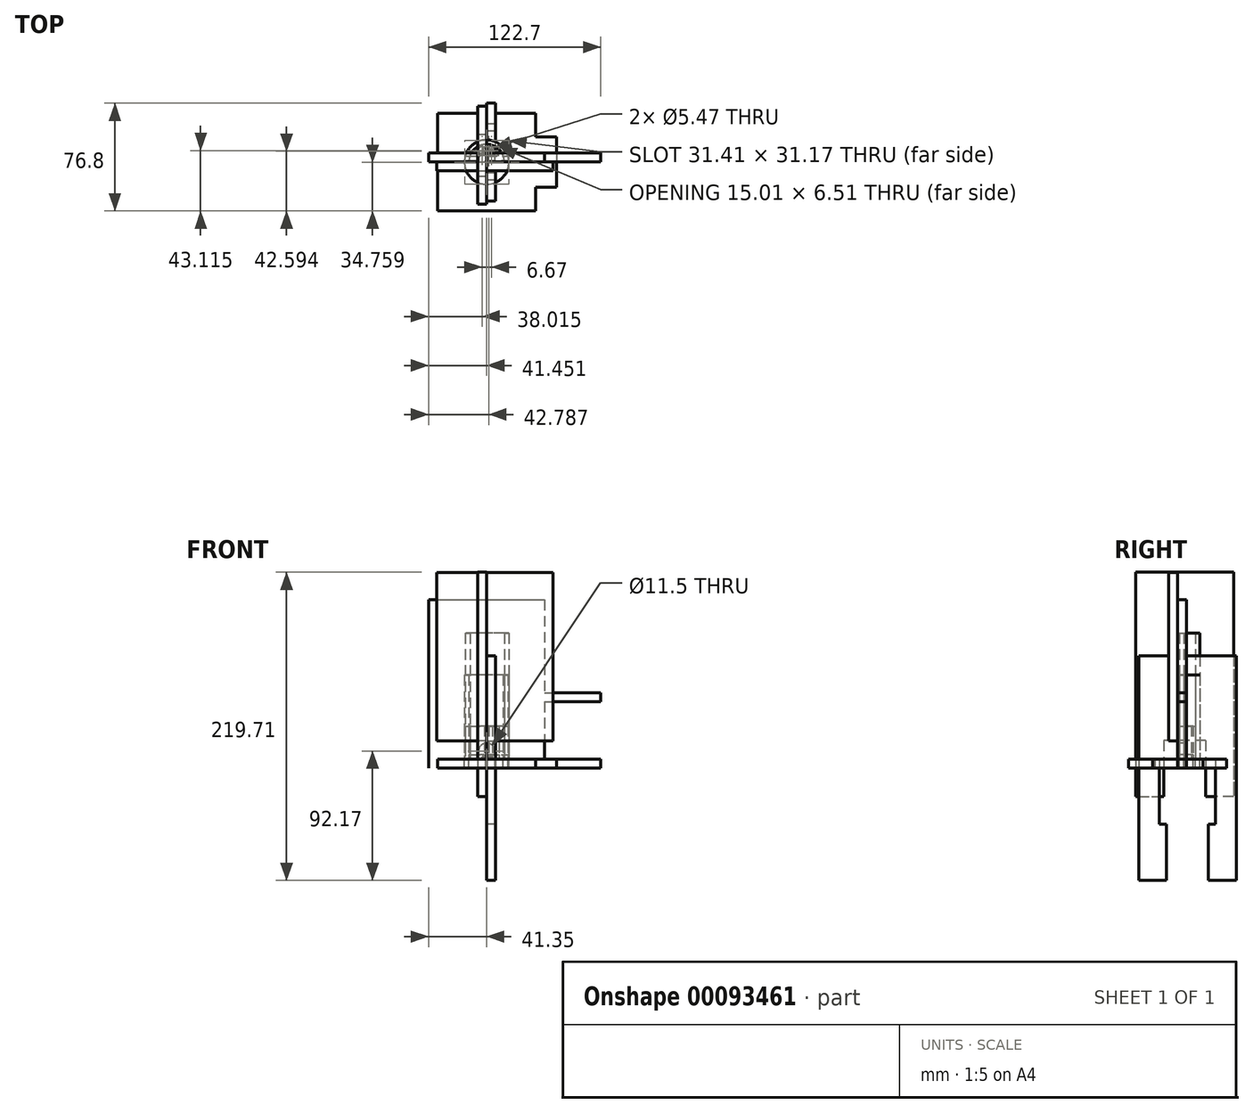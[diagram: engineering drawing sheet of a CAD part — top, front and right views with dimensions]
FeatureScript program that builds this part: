
annotation { "Feature Type Name" : "Feature", "Feature Type Description" : "" }
export const myFeature = defineFeature(function(context is Context, id is Id, definition is map)
    precondition{}
    {
        {
            var Q0;
            Q0=qCreatedBy(makeId("Top.planeOp"),FACE);
            var sketch = newSketch(context, id + "F0", { "sketchPlane" : qUnion([Q0])});
            skLineSegment(sketch, "E0.bottom", {"start": v(-34.9, 34.9) * mm, "end": v(34.9, 34.9) * mm});
            skLineSegment(sketch, "E0.top", {"start": v(-34.9, -34.9) * mm, "end": v(34.9, -34.9) * mm});
            skLineSegment(sketch, "E0.left", {"start": v(-34.9, 34.9) * mm, "end": v(-34.9, -34.9) * mm});
            skLineSegment(sketch, "E0.right", {"start": v(34.9, 34.9) * mm, "end": v(34.9, -34.9) * mm});
            skPoint(sketch, "E0.middle", {"position": v(0, 0) * mm});
            skCircle(sketch, "E1", {"center": v(0, 0) * mm, "radius": 15.85 * mm});
            skLineSegment(sketch, "E2.bottom", {"start": v(34.9, 18) * mm, "end": v(49.9, 18) * mm});
            skLineSegment(sketch, "E2.top", {"start": v(34.9, -18) * mm, "end": v(49.9, -18) * mm});
            skLineSegment(sketch, "E2.right", {"start": v(49.9, 18) * mm, "end": v(49.9, -18) * mm});
            skCircle(sketch, "E3", {"center": v(0, 0) * mm, "radius": 12.65 * mm});
            skPoint(sketch, "E4.startSnap0", {"position": v(-34.9, 0) * mm});
            skCircle(sketch, "E5", {"center": v(3.34, 8.21) * mm, "radius": 2.74 * mm});
            skCircle(sketch, "E6", {"center": v(-3.34, 8.21) * mm, "radius": 2.74 * mm});
            skCircle(sketch, "E7", {"center": v(0, 8.21) * mm, "radius": 2.74 * mm});
            skCircle(sketch, "E8", {"center": v(6.26, 7.15) * mm, "radius": 2.74 * mm});
            skLineSegment(sketch, "E9", {"start": v(3.63, 6.39) * mm, "end": v(8.89, 6.39) * mm});
            skLineSegment(sketch, "E10", {"start": v(-15.24, 4.35) * mm, "end": v(15.24, 4.35) * mm});
            skLineSegment(sketch, "E11", {"start": v(-15.8, 1.17) * mm, "end": v(15.8, 1.17) * mm});
            skSolve(sketch);
        }
        {
            var Q0;
            {var subQ0=sQuery(id+"F0.wireOp",EDGE,"E2.bottom");Q0=makeQuery(id+"F0.imprint","IMPRINT",FACE,{"disambiguationData":[TD([[makeQuery(id+"F0.imprint","IMPRINT",EDGE,{"derivedFrom":subQ0}),-1.0]])]});}
            var Q1;
            {var subQ1=sQuery(id+"F0.wireOp",EDGE,"E0.bottom");Q1=makeQuery(id+"F0.imprint","IMPRINT",FACE,{"disambiguationData":[TD([[makeQuery(id+"F0.imprint","IMPRINT",EDGE,{"derivedFrom":subQ1}),-1.0]])]});}
            var Q2;
            {var subQ0=sQuery(id+"F0.wireOp",EDGE,"E7");var subQ1=sQuery(id+"F0.wireOp",EDGE,"E5");var subQ2=makeQuery(id+"F0.imprint","INTERSECT",VERTEX,{"disambiguationData":[OD(0.0)],"derivedFrom":[subQ1,subQ0]});Q2=makeQuery(id+"F0.imprint","IMPRINT",FACE,{"disambiguationData":[TD([[makeQuery(id+"F0.imprint","IMPRINT",EDGE,{"disambiguationData":[TD([[subQ2,-1.0]])],"derivedFrom":subQ1}),-1.0]])]});}
            var Q3;
            {var subQ0=sQuery(id+"F0.wireOp",EDGE,"E8");var subQ1=sQuery(id+"F0.wireOp",EDGE,"E5");var subQ2=makeQuery(id+"F0.imprint","INTERSECT",VERTEX,{"disambiguationData":[OD(0.0)],"derivedFrom":[subQ1,subQ0]});Q3=makeQuery(id+"F0.imprint","IMPRINT",FACE,{"disambiguationData":[TD([[makeQuery(id+"F0.imprint","IMPRINT",EDGE,{"disambiguationData":[TD([[subQ2,1.0]])],"derivedFrom":subQ1}),-1.0]])]});}
            var Q4;
            {var subQ0=sQuery(id+"F0.wireOp",EDGE,"E10");var subQ1=sQuery(id+"F0.wireOp",EDGE,"E1");var subQ2=makeQuery(id+"F0.imprint","INTERSECT",VERTEX,{"disambiguationData":[OD(0.0)],"derivedFrom":[subQ1,subQ0]});Q4=makeQuery(id+"F0.imprint","IMPRINT",FACE,{"disambiguationData":[TD([[makeQuery(id+"F0.imprint","IMPRINT",EDGE,{"disambiguationData":[TD([[subQ2,1.0]])],"derivedFrom":subQ1}),1.0]])]});}
            var Q5;
            {var subQ11=sQuery(id+"F0.wireOp",EDGE,"E10");var subQ12=sQuery(id+"F0.wireOp",EDGE,"E3");var subQ13=makeQuery(id+"F0.imprint","INTERSECT",VERTEX,{"disambiguationData":[OD(0.0)],"derivedFrom":[subQ12,subQ11]});Q5=makeQuery(id+"F0.imprint","IMPRINT",FACE,{"disambiguationData":[TD([[makeQuery(id+"F0.imprint","IMPRINT",EDGE,{"disambiguationData":[TD([[subQ13,-1.0]])],"derivedFrom":subQ12}),1.0]])]});}
            var Q6;
            {var subQ0=sQuery(id+"F0.wireOp",EDGE,"E10");var subQ1=sQuery(id+"F0.wireOp",EDGE,"E3");var subQ2=makeQuery(id+"F0.imprint","INTERSECT",VERTEX,{"disambiguationData":[OD(0.0)],"derivedFrom":[subQ1,subQ0]});Q6=makeQuery(id+"F0.imprint","IMPRINT",FACE,{"disambiguationData":[TD([[makeQuery(id+"F0.imprint","IMPRINT",EDGE,{"disambiguationData":[TD([[subQ2,1.0]])],"derivedFrom":subQ1}),1.0]])]});}
            var Q7;
            {var subQ0=sQuery(id+"F0.wireOp",EDGE,"E8");var subQ1=sQuery(id+"F0.wireOp",EDGE,"E5");var subQ2=makeQuery(id+"F0.imprint","INTERSECT",VERTEX,{"disambiguationData":[OD(1.0)],"derivedFrom":[subQ1,subQ0]});Q7=makeQuery(id+"F0.imprint","IMPRINT",FACE,{"disambiguationData":[TD([[makeQuery(id+"F0.imprint","IMPRINT",EDGE,{"disambiguationData":[TD([[subQ2,-1.0]])],"derivedFrom":subQ1}),-1.0]])]});}
            extrude(context, id + "F1", {"entities" : qUnion([Q0, Q1, Q2, Q3, Q4, Q5, Q6, Q7]), "oppositeDirection" : true, "depth" : 6.35 * mm});
        }
        {
            var Q0;
            Q0=qCreatedBy(makeId("Front.planeOp"),FACE);
            var sketch = newSketch(context, id + "F2", { "sketchPlane" : qUnion([Q0])});
            skLineSegment(sketch, "E12.bottom", {"start": v(-35.54, 133.25) * mm, "end": v(47.16, 133.25) * mm});
            skLineSegment(sketch, "E12.top", {"start": v(-35.54, 13.25) * mm, "end": v(47.16, 13.25) * mm});
            skLineSegment(sketch, "E12.left", {"start": v(-35.54, 133.25) * mm, "end": v(-35.54, 13.25) * mm});
            skLineSegment(sketch, "E12.right", {"start": v(47.16, 133.25) * mm, "end": v(47.16, 13.25) * mm});
            skLineSegment(sketch, "E13.bottom", {"start": v(-35.54, 13.25) * mm, "end": v(-9.2, 13.25) * mm});
            skLineSegment(sketch, "E13.top", {"start": v(-35.54, -26.75) * mm, "end": v(-9.2, -26.75) * mm});
            skLineSegment(sketch, "E13.left", {"start": v(-35.54, 13.25) * mm, "end": v(-35.54, -26.75) * mm});
            skLineSegment(sketch, "E13.right", {"start": v(-9.2, 13.25) * mm, "end": v(-9.2, -26.75) * mm});
            skLineSegment(sketch, "E14.bottom", {"start": v(47.16, 13.25) * mm, "end": v(20.8, 13.25) * mm});
            skLineSegment(sketch, "E14.top", {"start": v(47.16, -26.75) * mm, "end": v(20.8, -26.75) * mm});
            skLineSegment(sketch, "E14.left", {"start": v(47.16, 13.25) * mm, "end": v(47.16, -26.75) * mm});
            skLineSegment(sketch, "E14.right", {"start": v(20.8, 13.25) * mm, "end": v(20.8, -26.75) * mm});
            skSolve(sketch);
        }
        {
            var Q0;
            Q0=makeQuery(id+"F2.imprint","IMPRINT",FACE,{"disambiguationData":[TD([[makeQuery(id+"F2.imprint","IMPRINT",EDGE,{"derivedFrom":sQuery(id+"F2.wireOp",EDGE,"E13.bottom")}),-1.0]])]});
            var Q1;
            Q1=makeQuery(id+"F2.imprint","IMPRINT",FACE,{"disambiguationData":[TD([[makeQuery(id+"F2.imprint","IMPRINT",EDGE,{"derivedFrom":sQuery(id+"F2.wireOp",EDGE,"E14.bottom")}),1.0]])]});
            var Q2;
            Q2=makeQuery(id+"F2.imprint","IMPRINT",FACE,{"disambiguationData":[TD([[makeQuery(id+"F2.imprint","IMPRINT",EDGE,{"derivedFrom":sQuery(id+"F2.wireOp",EDGE,"E12.bottom")}),-1.0]])]});
            extrude(context, id + "F3", {"entities" : qUnion([Q0, Q1, Q2]), "depth" : 6.35 * mm});
        }
        {
            var Q0;
            Q0=qCreatedBy(makeId("Front.planeOp"),FACE);
            var sketch = newSketch(context, id + "F4", { "sketchPlane" : qUnion([Q0])});
            skLineSegment(sketch, "E15.bottom", {"start": v(-41.35, 113.65) * mm, "end": v(41.35, 113.65) * mm});
            skLineSegment(sketch, "E15.top", {"start": v(-41.35, -6.35) * mm, "end": v(41.35, -6.35) * mm});
            skLineSegment(sketch, "E15.left", {"start": v(-41.35, 113.65) * mm, "end": v(-41.35, -6.35) * mm});
            skLineSegment(sketch, "E15.right", {"start": v(41.35, 113.65) * mm, "end": v(41.35, -6.35) * mm});
            skLineSegment(sketch, "E16.bottom", {"start": v(-41.35, -6.35) * mm, "end": v(-15, -6.35) * mm});
            skLineSegment(sketch, "E16.top", {"start": v(-41.35, -46.35) * mm, "end": v(-15, -46.35) * mm});
            skLineSegment(sketch, "E16.left", {"start": v(-41.35, -6.35) * mm, "end": v(-41.35, -46.35) * mm});
            skLineSegment(sketch, "E16.right", {"start": v(-15, -6.35) * mm, "end": v(-15, -46.35) * mm});
            skLineSegment(sketch, "E17.bottom", {"start": v(41.35, -6.35) * mm, "end": v(15, -6.35) * mm});
            skLineSegment(sketch, "E17.top", {"start": v(41.35, -46.35) * mm, "end": v(15, -46.35) * mm});
            skLineSegment(sketch, "E17.left", {"start": v(41.35, -6.35) * mm, "end": v(41.35, -46.35) * mm});
            skLineSegment(sketch, "E17.right", {"start": v(15, -6.35) * mm, "end": v(15, -46.35) * mm});
            skCircle(sketch, "E18", {"center": v(0, 5.8) * mm, "radius": 5.75 * mm});
            skLineSegment(sketch, "E19.bottom", {"start": v(41.35, -6.35) * mm, "end": v(81.35, -6.35) * mm});
            skLineSegment(sketch, "E19.top", {"start": v(41.35, 47.35) * mm, "end": v(81.35, 47.35) * mm});
            skLineSegment(sketch, "E19.left", {"start": v(41.35, -6.35) * mm, "end": v(41.35, 47.35) * mm});
            skLineSegment(sketch, "E19.right", {"start": v(81.35, -6.35) * mm, "end": v(81.35, 47.35) * mm});
            skLineSegment(sketch, "E20.bottom", {"start": v(41.35, 41) * mm, "end": v(81.35, 41) * mm});
            skLineSegment(sketch, "E20.top", {"start": v(41.35, 0) * mm, "end": v(81.35, 0) * mm});
            skLineSegment(sketch, "E20.left", {"start": v(41.35, 41) * mm, "end": v(41.35, 0) * mm});
            skLineSegment(sketch, "E20.right", {"start": v(81.35, 41) * mm, "end": v(81.35, 0) * mm});
            skSolve(sketch);
        }
        {
            var Q0;
            Q0=makeQuery(id+"F4.imprint","IMPRINT",FACE,{"disambiguationData":[TD([[makeQuery(id+"F4.imprint","IMPRINT",EDGE,{"derivedFrom":sQuery(id+"F4.wireOp",EDGE,"E16.bottom")}),-1.0]])]});
            var Q1;
            Q1=makeQuery(id+"F4.imprint","IMPRINT",FACE,{"disambiguationData":[TD([[makeQuery(id+"F4.imprint","IMPRINT",EDGE,{"derivedFrom":sQuery(id+"F4.wireOp",EDGE,"E17.bottom")}),1.0]])]});
            var Q2;
            Q2=makeQuery(id+"F4.imprint","IMPRINT",FACE,{"disambiguationData":[TD([[makeQuery(id+"F4.imprint","IMPRINT",EDGE,{"derivedFrom":sQuery(id+"F4.wireOp",EDGE,"E15.bottom")}),-1.0]])]});
            var Q3;
            {var subQ0=sQuery(id+"F4.wireOp",EDGE,"E19.bottom");Q3=makeQuery(id+"F4.imprint","IMPRINT",FACE,{"disambiguationData":[TD([[makeQuery(id+"F4.imprint","IMPRINT",EDGE,{"derivedFrom":subQ0}),1.0]])]});}
            var Q4;
            {var subQ0=sQuery(id+"F4.wireOp",EDGE,"E19.top");Q4=makeQuery(id+"F4.imprint","IMPRINT",FACE,{"disambiguationData":[TD([[makeQuery(id+"F4.imprint","IMPRINT",EDGE,{"derivedFrom":subQ0}),-1.0]])]});}
            extrude(context, id + "F5", {"entities" : qUnion([Q0, Q1, Q2, Q3, Q4]), "oppositeDirection" : true, "depth" : 6.35 * mm});
        }
        {
            var Q0;
            Q0=qCreatedBy(makeId("Right.planeOp"),FACE);
            var sketch = newSketch(context, id + "F6", { "sketchPlane" : qUnion([Q0])});
            skLineSegment(sketch, "E21.bottom", {"start": v(39.82, 133.34) * mm, "end": v(-29.98, 133.34) * mm});
            skLineSegment(sketch, "E21.top", {"start": v(39.82, 13.34) * mm, "end": v(-29.98, 13.34) * mm});
            skLineSegment(sketch, "E21.left", {"start": v(39.82, 133.34) * mm, "end": v(39.82, 13.34) * mm});
            skLineSegment(sketch, "E21.right", {"start": v(-29.98, 133.34) * mm, "end": v(-29.98, 13.34) * mm});
            skLineSegment(sketch, "E22.bottom", {"start": v(39.82, 13.34) * mm, "end": v(19.82, 13.34) * mm});
            skLineSegment(sketch, "E22.top", {"start": v(39.82, -26.66) * mm, "end": v(19.82, -26.66) * mm});
            skLineSegment(sketch, "E22.left", {"start": v(39.82, 13.34) * mm, "end": v(39.82, -26.66) * mm});
            skLineSegment(sketch, "E22.right", {"start": v(19.82, 13.34) * mm, "end": v(19.82, -26.66) * mm});
            skLineSegment(sketch, "E23.bottom", {"start": v(-29.98, 13.34) * mm, "end": v(-9.98, 13.34) * mm});
            skLineSegment(sketch, "E23.top", {"start": v(-29.98, -26.66) * mm, "end": v(-9.98, -26.66) * mm});
            skLineSegment(sketch, "E23.left", {"start": v(-29.98, 13.34) * mm, "end": v(-29.98, -26.66) * mm});
            skLineSegment(sketch, "E23.right", {"start": v(-9.98, 13.34) * mm, "end": v(-9.98, -26.66) * mm});
            skSolve(sketch);
        }
        {
            var Q0;
            Q0 = qSketchRegion(id + "F6", true);
            extrude(context, id + "F7", {"entities" : qUnion([Q0]), "oppositeDirection" : true, "depth" : 6.35 * mm});
        }
        {
            var Q0;
            Q0=qCreatedBy(makeId("Right.planeOp"),FACE);
            var sketch = newSketch(context, id + "F8", { "sketchPlane" : qUnion([Q0])});
            skLineSegment(sketch, "E24.bottom", {"start": v(-27.9, 73.63) * mm, "end": v(41.9, 73.63) * mm});
            skLineSegment(sketch, "E24.top", {"start": v(-27.9, -46.37) * mm, "end": v(41.9, -46.37) * mm});
            skLineSegment(sketch, "E24.left", {"start": v(-27.9, 73.63) * mm, "end": v(-27.9, -46.37) * mm});
            skLineSegment(sketch, "E24.right", {"start": v(41.9, 73.63) * mm, "end": v(41.9, -46.37) * mm});
            skLineSegment(sketch, "E25.bottom", {"start": v(-13, 0) * mm, "end": v(27, 0) * mm});
            skLineSegment(sketch, "E25.top", {"start": v(-13, -46.37) * mm, "end": v(27, -46.37) * mm});
            skLineSegment(sketch, "E25.left", {"start": v(-13, 0) * mm, "end": v(-13, -46.37) * mm});
            skLineSegment(sketch, "E25.right", {"start": v(27, 0) * mm, "end": v(27, -46.37) * mm});
            skLineSegment(sketch, "E26.bottom", {"start": v(-27.9, -46.37) * mm, "end": v(-7.9, -46.37) * mm});
            skLineSegment(sketch, "E26.top", {"start": v(-27.9, -86.37) * mm, "end": v(-7.9, -86.37) * mm});
            skLineSegment(sketch, "E26.left", {"start": v(-27.9, -46.37) * mm, "end": v(-27.9, -86.37) * mm});
            skLineSegment(sketch, "E26.right", {"start": v(-7.9, -46.37) * mm, "end": v(-7.9, -86.37) * mm});
            skLineSegment(sketch, "E27.bottom", {"start": v(41.9, -46.37) * mm, "end": v(21.9, -46.37) * mm});
            skLineSegment(sketch, "E27.top", {"start": v(41.9, -86.37) * mm, "end": v(21.9, -86.37) * mm});
            skLineSegment(sketch, "E27.left", {"start": v(41.9, -46.37) * mm, "end": v(41.9, -86.37) * mm});
            skLineSegment(sketch, "E27.right", {"start": v(21.9, -46.37) * mm, "end": v(21.9, -86.37) * mm});
            skSolve(sketch);
        }
        {
            var Q0;
            Q0=makeQuery(id+"F8.imprint","IMPRINT",FACE,{"disambiguationData":[TD([[makeQuery(id+"F8.imprint","IMPRINT",EDGE,{"derivedFrom":sQuery(id+"F8.wireOp",EDGE,"E26.top")}),1.0]])]});
            var Q1;
            Q1=makeQuery(id+"F8.imprint","IMPRINT",FACE,{"disambiguationData":[TD([[makeQuery(id+"F8.imprint","IMPRINT",EDGE,{"derivedFrom":sQuery(id+"F8.wireOp",EDGE,"E27.top")}),-1.0]])]});
            var Q2;
            Q2=makeQuery(id+"F8.imprint","IMPRINT",FACE,{"disambiguationData":[TD([[makeQuery(id+"F8.imprint","IMPRINT",EDGE,{"derivedFrom":sQuery(id+"F8.wireOp",EDGE,"E24.bottom")}),-1.0]])]});
            extrude(context, id + "F9", {"entities" : qUnion([Q0, Q1, Q2]), "depth" : 6.35 * mm});
        }
        {
            var Q0;
            {var subQ0=sQuery(id+"F0.wireOp",EDGE,"E10");var subQ1=sQuery(id+"F0.wireOp",EDGE,"E1");var subQ2=makeQuery(id+"F0.imprint","INTERSECT",VERTEX,{"disambiguationData":[OD(0.0)],"derivedFrom":[subQ1,subQ0]});Q0=makeQuery(id+"F0.imprint","IMPRINT",FACE,{"disambiguationData":[TD([[makeQuery(id+"F0.imprint","IMPRINT",EDGE,{"disambiguationData":[TD([[subQ2,1.0]])],"derivedFrom":subQ1}),1.0]])]});}
            var Q1;
            {var subQ0=sQuery(id+"F0.wireOp",EDGE,"E10");var subQ1=sQuery(id+"F0.wireOp",EDGE,"E1");var subQ2=makeQuery(id+"F0.imprint","INTERSECT",VERTEX,{"disambiguationData":[OD(1.0)],"derivedFrom":[subQ1,subQ0]});Q1=makeQuery(id+"F0.imprint","IMPRINT",FACE,{"disambiguationData":[TD([[makeQuery(id+"F0.imprint","IMPRINT",EDGE,{"disambiguationData":[TD([[subQ2,-1.0]])],"derivedFrom":subQ1}),1.0]])]});}
            var Q2;
            {var subQ0=sQuery(id+"F0.wireOp",EDGE,"E10");var subQ1=sQuery(id+"F0.wireOp",EDGE,"E1");var subQ2=makeQuery(id+"F0.imprint","INTERSECT",VERTEX,{"disambiguationData":[OD(0.0)],"derivedFrom":[subQ1,subQ0]});Q2=makeQuery(id+"F0.imprint","IMPRINT",FACE,{"disambiguationData":[TD([[makeQuery(id+"F0.imprint","IMPRINT",EDGE,{"disambiguationData":[TD([[subQ2,1.0]])],"derivedFrom":subQ1}),1.0]])]});}
            var Q3;
            {var subQ0=sQuery(id+"F0.wireOp",EDGE,"E10");var subQ1=sQuery(id+"F0.wireOp",EDGE,"E1");var subQ2=makeQuery(id+"F0.imprint","INTERSECT",VERTEX,{"disambiguationData":[OD(0.0)],"derivedFrom":[subQ1,subQ0]});Q3=makeQuery(id+"F0.imprint","IMPRINT",FACE,{"disambiguationData":[TD([[makeQuery(id+"F0.imprint","IMPRINT",EDGE,{"disambiguationData":[TD([[subQ2,1.0]])],"derivedFrom":subQ1}),1.0]])]});}
            var Q4;
            {var subQ0=sQuery(id+"F0.wireOp",EDGE,"E10");var subQ1=sQuery(id+"F0.wireOp",EDGE,"E1");var subQ2=makeQuery(id+"F0.imprint","INTERSECT",VERTEX,{"disambiguationData":[OD(1.0)],"derivedFrom":[subQ1,subQ0]});Q4=makeQuery(id+"F0.imprint","IMPRINT",FACE,{"disambiguationData":[TD([[makeQuery(id+"F0.imprint","IMPRINT",EDGE,{"disambiguationData":[TD([[subQ2,-1.0]])],"derivedFrom":subQ1}),1.0]])]});}
            var Q5;
            {var subQ0=sQuery(id+"F0.wireOp",EDGE,"n6fMbl8c-e2gG-Q103-9a3W-R0qhI9RANw06");var subQ1=sQuery(id+"F0.wireOp",EDGE,"E3");var subQ2=makeQuery(id+"F0.imprint","INTERSECT",VERTEX,{"disambiguationData":[OD(0.0)],"derivedFrom":[subQ1,subQ0]});Q5=makeQuery(id+"F0.imprint","IMPRINT",FACE,{"disambiguationData":[TD([[makeQuery(id+"F0.imprint","IMPRINT",EDGE,{"disambiguationData":[TD([[subQ2,1.0]])],"derivedFrom":subQ1}),1.0]])]});}
            var Q6;
            {var subQ0=sQuery(id+"F0.wireOp",EDGE,"n6fMbl8c-e2gG-Q103-9a3W-R0qhI9RANw06");var subQ1=sQuery(id+"F0.wireOp",EDGE,"E8");var subQ2=makeQuery(id+"F0.imprint","INTERSECT",VERTEX,{"disambiguationData":[OD(0.0)],"derivedFrom":[subQ1,subQ0]});Q6=makeQuery(id+"F0.imprint","IMPRINT",FACE,{"disambiguationData":[TD([[makeQuery(id+"F0.imprint","IMPRINT",EDGE,{"disambiguationData":[TD([[subQ2,-1.0]])],"derivedFrom":subQ1}),1.0]])]});}
            extrude(context, id + "F10", {"entities" : qUnion([Q0, Q1, Q2, Q3, Q4, Q5, Q6]), "depth" : 23.7 * mm});
        }
        {
            var Q0;
            {var subQ0=sQuery(id+"F0.wireOp",EDGE,"E10");var subQ1=sQuery(id+"F0.wireOp",EDGE,"E1");var subQ2=makeQuery(id+"F0.imprint","INTERSECT",VERTEX,{"disambiguationData":[OD(0.0)],"derivedFrom":[subQ1,subQ0]});Q0=makeQuery(id+"F0.imprint","IMPRINT",FACE,{"disambiguationData":[TD([[makeQuery(id+"F0.imprint","IMPRINT",EDGE,{"disambiguationData":[TD([[subQ2,1.0]])],"derivedFrom":subQ1}),1.0]])]});}
            var Q1;
            {var subQ0=sQuery(id+"F0.wireOp",EDGE,"E10");var subQ1=sQuery(id+"F0.wireOp",EDGE,"E1");var subQ2=makeQuery(id+"F0.imprint","INTERSECT",VERTEX,{"disambiguationData":[OD(0.0)],"derivedFrom":[subQ1,subQ0]});Q1=makeQuery(id+"F0.imprint","IMPRINT",FACE,{"disambiguationData":[TD([[makeQuery(id+"F0.imprint","IMPRINT",EDGE,{"disambiguationData":[TD([[subQ2,1.0]])],"derivedFrom":subQ1}),1.0]])]});}
            var Q2;
            {var subQ0=sQuery(id+"F0.wireOp",EDGE,"E7");var subQ1=sQuery(id+"F0.wireOp",EDGE,"E6");var subQ2=makeQuery(id+"F0.imprint","INTERSECT",VERTEX,{"disambiguationData":[OD(0.0)],"derivedFrom":[subQ1,subQ0]});Q2=makeQuery(id+"F0.imprint","IMPRINT",FACE,{"disambiguationData":[TD([[makeQuery(id+"F0.imprint","IMPRINT",EDGE,{"disambiguationData":[TD([[subQ2,-1.0]])],"derivedFrom":subQ1}),1.0]])]});}
            var Q3;
            {var subQ2=sQuery(id+"F0.wireOp",EDGE,"E5");var subQ4=sQuery(id+"F0.wireOp",EDGE,"E7");var subQ5=makeQuery(id+"F0.imprint","INTERSECT",VERTEX,{"disambiguationData":[OD(0.0)],"derivedFrom":[subQ2,subQ4]});Q3=makeQuery(id+"F0.imprint","IMPRINT",FACE,{"disambiguationData":[TD([[makeQuery(id+"F0.imprint","IMPRINT",EDGE,{"disambiguationData":[TD([[subQ5,1.0]])],"derivedFrom":subQ2}),1.0]])]});}
            var Q4;
            {var subQ0=sQuery(id+"F0.wireOp",EDGE,"E8");var subQ1=sQuery(id+"F0.wireOp",EDGE,"E5");var subQ2=makeQuery(id+"F0.imprint","INTERSECT",VERTEX,{"disambiguationData":[OD(1.0)],"derivedFrom":[subQ1,subQ0]});Q4=makeQuery(id+"F0.imprint","IMPRINT",FACE,{"disambiguationData":[TD([[makeQuery(id+"F0.imprint","IMPRINT",EDGE,{"disambiguationData":[TD([[subQ2,-1.0]])],"derivedFrom":subQ1}),1.0]])]});}
            var Q5;
            {var subQ0=sQuery(id+"F0.wireOp",EDGE,"E8");var subQ1=sQuery(id+"F0.wireOp",EDGE,"E5");var subQ2=makeQuery(id+"F0.imprint","INTERSECT",VERTEX,{"disambiguationData":[OD(1.0)],"derivedFrom":[subQ1,subQ0]});Q5=makeQuery(id+"F0.imprint","IMPRINT",FACE,{"disambiguationData":[TD([[makeQuery(id+"F0.imprint","IMPRINT",EDGE,{"disambiguationData":[TD([[subQ2,-1.0]])],"derivedFrom":subQ1}),1.0]])]});}
            var Q6;
            {var subQ0=sQuery(id+"F0.wireOp",EDGE,"E10");var subQ1=sQuery(id+"F0.wireOp",EDGE,"E1");var subQ2=makeQuery(id+"F0.imprint","INTERSECT",VERTEX,{"disambiguationData":[OD(0.0)],"derivedFrom":[subQ1,subQ0]});Q6=makeQuery(id+"F0.imprint","IMPRINT",FACE,{"disambiguationData":[TD([[makeQuery(id+"F0.imprint","IMPRINT",EDGE,{"disambiguationData":[TD([[subQ2,1.0]])],"derivedFrom":subQ1}),1.0]])]});}
            var Q7;
            {var subQ11=sQuery(id+"F0.wireOp",EDGE,"E10");var subQ12=sQuery(id+"F0.wireOp",EDGE,"E3");var subQ13=makeQuery(id+"F0.imprint","INTERSECT",VERTEX,{"disambiguationData":[OD(0.0)],"derivedFrom":[subQ12,subQ11]});Q7=makeQuery(id+"F0.imprint","IMPRINT",FACE,{"disambiguationData":[TD([[makeQuery(id+"F0.imprint","IMPRINT",EDGE,{"disambiguationData":[TD([[subQ13,-1.0]])],"derivedFrom":subQ12}),1.0]])]});}
            var Q8;
            {var subQ0=sQuery(id+"F0.wireOp",EDGE,"E8");var subQ1=sQuery(id+"F0.wireOp",EDGE,"E5");var subQ2=makeQuery(id+"F0.imprint","INTERSECT",VERTEX,{"disambiguationData":[OD(1.0)],"derivedFrom":[subQ1,subQ0]});Q8=makeQuery(id+"F0.imprint","IMPRINT",FACE,{"disambiguationData":[TD([[makeQuery(id+"F0.imprint","IMPRINT",EDGE,{"disambiguationData":[TD([[subQ2,-1.0]])],"derivedFrom":subQ1}),-1.0]])]});}
            extrude(context, id + "F11", {"entities" : qUnion([Q0, Q1, Q2, Q3, Q4, Q5, Q6, Q7, Q8]), "depth" : 3.17 * mm});
        }
        {
            var Q0;
            {var subQ0=sQuery(id+"F0.wireOp",EDGE,"E10");var subQ1=sQuery(id+"F0.wireOp",EDGE,"E3");var subQ2=makeQuery(id+"F0.imprint","INTERSECT",VERTEX,{"disambiguationData":[OD(0.0)],"derivedFrom":[subQ1,subQ0]});Q0=makeQuery(id+"F0.imprint","IMPRINT",FACE,{"disambiguationData":[TD([[makeQuery(id+"F0.imprint","IMPRINT",EDGE,{"disambiguationData":[TD([[subQ2,1.0]])],"derivedFrom":subQ1}),1.0]])]});}
            extrude(context, id + "F12", {"entities" : qUnion([Q0]), "depth" : 23.65 * mm});
        }
        {
            var Q0;
            {var subQ0=sQuery(id+"F0.wireOp",EDGE,"E10");var subQ1=sQuery(id+"F0.wireOp",EDGE,"E1");var subQ2=makeQuery(id+"F0.imprint","INTERSECT",VERTEX,{"disambiguationData":[OD(0.0)],"derivedFrom":[subQ1,subQ0]});Q0=makeQuery(id+"F0.imprint","IMPRINT",FACE,{"disambiguationData":[TD([[makeQuery(id+"F0.imprint","IMPRINT",EDGE,{"disambiguationData":[TD([[subQ2,1.0]])],"derivedFrom":subQ1}),1.0]])]});}
            var Q1;
            {var subQ0=sQuery(id+"F0.wireOp",EDGE,"E10");var subQ1=sQuery(id+"F0.wireOp",EDGE,"E1");var subQ2=makeQuery(id+"F0.imprint","INTERSECT",VERTEX,{"disambiguationData":[OD(0.0)],"derivedFrom":[subQ1,subQ0]});Q1=makeQuery(id+"F0.imprint","IMPRINT",FACE,{"disambiguationData":[TD([[makeQuery(id+"F0.imprint","IMPRINT",EDGE,{"disambiguationData":[TD([[subQ2,-1.0]])],"derivedFrom":subQ1}),1.0]])]});}
            var Q2;
            {var subQ0=sQuery(id+"F0.wireOp",EDGE,"E10");var subQ1=sQuery(id+"F0.wireOp",EDGE,"E1");var subQ2=makeQuery(id+"F0.imprint","INTERSECT",VERTEX,{"disambiguationData":[OD(1.0)],"derivedFrom":[subQ1,subQ0]});Q2=makeQuery(id+"F0.imprint","IMPRINT",FACE,{"disambiguationData":[TD([[makeQuery(id+"F0.imprint","IMPRINT",EDGE,{"disambiguationData":[TD([[subQ2,-1.0]])],"derivedFrom":subQ1}),1.0]])]});}
            var Q3;
            {var subQ0=sQuery(id+"F0.wireOp",EDGE,"n6fMbl8c-e2gG-Q103-9a3W-R0qhI9RANw06");var subQ1=sQuery(id+"F0.wireOp",EDGE,"E1");var subQ2=makeQuery(id+"F0.imprint","INTERSECT",VERTEX,{"disambiguationData":[OD(0.0)],"derivedFrom":[subQ1,subQ0]});Q3=makeQuery(id+"F0.imprint","IMPRINT",FACE,{"disambiguationData":[TD([[makeQuery(id+"F0.imprint","IMPRINT",EDGE,{"disambiguationData":[TD([[subQ2,1.0]])],"derivedFrom":subQ1}),1.0]])]});}
            extrude(context, id + "F13", {"entities" : qUnion([Q0, Q1, Q2, Q3]), "depth" : 60 * mm});
        }
        {
            var Q0;
            {var subQ0=sQuery(id+"F0.wireOp",EDGE,"E10");var subQ1=sQuery(id+"F0.wireOp",EDGE,"E1");var subQ2=makeQuery(id+"F0.imprint","INTERSECT",VERTEX,{"disambiguationData":[OD(0.0)],"derivedFrom":[subQ1,subQ0]});Q0=makeQuery(id+"F0.imprint","IMPRINT",FACE,{"disambiguationData":[TD([[makeQuery(id+"F0.imprint","IMPRINT",EDGE,{"disambiguationData":[TD([[subQ2,-1.0]])],"derivedFrom":subQ1}),1.0]])]});}
            var Q1;
            {var subQ0=sQuery(id+"F0.wireOp",EDGE,"E11");var subQ1=sQuery(id+"F0.wireOp",EDGE,"E1");var subQ2=makeQuery(id+"F0.imprint","INTERSECT",VERTEX,{"disambiguationData":[OD(0.0)],"derivedFrom":[subQ1,subQ0]});Q1=makeQuery(id+"F0.imprint","IMPRINT",FACE,{"disambiguationData":[TD([[makeQuery(id+"F0.imprint","IMPRINT",EDGE,{"disambiguationData":[TD([[subQ2,-1.0]])],"derivedFrom":subQ1}),1.0]])]});}
            var Q2;
            {var subQ0=sQuery(id+"F0.wireOp",EDGE,"E10");var subQ1=sQuery(id+"F0.wireOp",EDGE,"E1");var subQ2=makeQuery(id+"F0.imprint","INTERSECT",VERTEX,{"disambiguationData":[OD(1.0)],"derivedFrom":[subQ1,subQ0]});Q2=makeQuery(id+"F0.imprint","IMPRINT",FACE,{"disambiguationData":[TD([[makeQuery(id+"F0.imprint","IMPRINT",EDGE,{"disambiguationData":[TD([[subQ2,1.0]])],"derivedFrom":subQ1}),1.0]])]});}
            extrude(context, id + "F14", {"entities" : qUnion([Q0, Q1, Q2]), "depth" : 90 * mm});
        }
        {
            var Q0;
            {var subQ0=sQuery(id+"F0.wireOp",EDGE,"E10");var subQ1=sQuery(id+"F0.wireOp",EDGE,"E1");var subQ2=makeQuery(id+"F0.imprint","INTERSECT",VERTEX,{"disambiguationData":[OD(0.0)],"derivedFrom":[subQ1,subQ0]});Q0=makeQuery(id+"F0.imprint","IMPRINT",FACE,{"disambiguationData":[TD([[makeQuery(id+"F0.imprint","IMPRINT",EDGE,{"disambiguationData":[TD([[subQ2,1.0]])],"derivedFrom":subQ1}),1.0]])]});}
            extrude(context, id + "F15", {"entities" : qUnion([Q0]), "depth" : 60 * mm});
        }
    });
